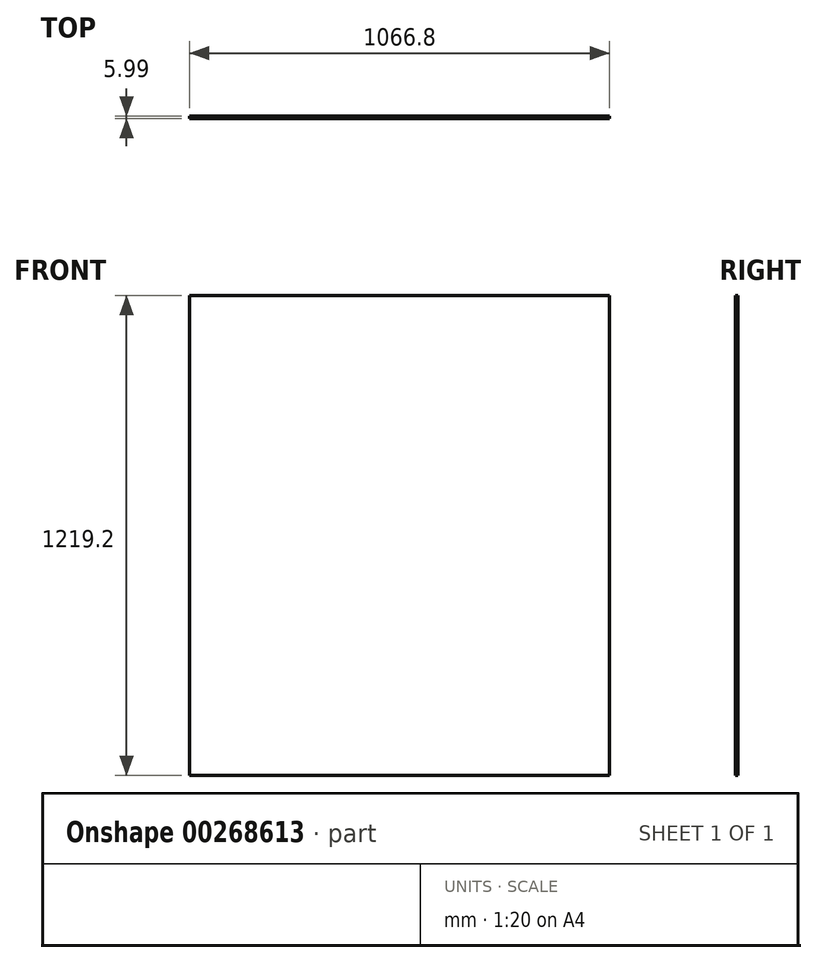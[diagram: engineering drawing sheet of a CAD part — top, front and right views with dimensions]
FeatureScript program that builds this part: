
annotation { "Feature Type Name" : "Feature", "Feature Type Description" : "" }
export const myFeature = defineFeature(function(context is Context, id is Id, definition is map)
    precondition{}
    {
        {
            var Q0;
            Q0=qCreatedBy(makeId("Front.planeOp"),FACE);
            var sketch = newSketch(context, id + "F0", { "sketchPlane" : qUnion([Q0])});
            skLineSegment(sketch, "E0.bottom", {"start": v(533.4, -609.6) * mm, "end": v(-533.4, -609.6) * mm});
            skLineSegment(sketch, "E0.top", {"start": v(533.4, 609.6) * mm, "end": v(-533.4, 609.6) * mm});
            skLineSegment(sketch, "E0.left", {"start": v(533.4, -609.6) * mm, "end": v(533.4, 609.6) * mm});
            skLineSegment(sketch, "E0.right", {"start": v(-533.4, -609.6) * mm, "end": v(-533.4, 609.6) * mm});
            skPoint(sketch, "E0.middle", {"position": v(0, 0) * mm});
            skSolve(sketch);
        }
        {
            var Q0;
            Q0=makeQuery(id+"F0.imprint","IMPRINT",FACE,{"disambiguationData":[TD([[makeQuery(id+"F0.imprint","IMPRINT",EDGE,{"derivedFrom":sQuery(id+"F0.wireOp",EDGE,"E0.bottom")}),-1.0]])]});
            extrude(context, id + "F1", {"entities" : qUnion([Q0]), "depth" : 6 * mm});
        }
    });
